annotation { "Feature Type Name" : "Feature", "Feature Type Description" : "" }
export const myFeature = defineFeature(function(context is Context, id is Id, definition is map)
    precondition{}
    {
        {
            var Q0;
            Q0=qCreatedBy(makeId("Top.planeOp"),FACE);
            var sketch = newSketch(context, id + "F0", { "sketchPlane" : qUnion([Q0])});
            skLineSegment(sketch, "E0.bottom", {"start": v(10900, -12400) * mm, "end": v(-10900, -12400) * mm});
            skLineSegment(sketch, "E0.top", {"start": v(10900, 12400) * mm, "end": v(-10900, 12400) * mm});
            skLineSegment(sketch, "E0.left", {"start": v(10900, -12400) * mm, "end": v(10900, 12400) * mm});
            skLineSegment(sketch, "E0.right", {"start": v(-10900, -12400) * mm, "end": v(-10900, 12400) * mm});
            skPoint(sketch, "E0.middle", {"position": v(0, 0) * mm});
            skSolve(sketch);
        }
        {
            var Q0;
            Q0=qSketchRegion(id+"F0",true);
            extrude(context, id + "F1", {"entities" : qUnion([Q0]), "depth" : 1000 * mm});
        }
        {
            var Q0;
            {var subQ2=sQuery(id+"FY67IvhjNhSzuPv_1.wireOp",EDGE,"VcfzDPvy-8ap2-iydv-9Ytp-1fS7yPx6LH9c.top");Q0=makeQuery(id+"FlI6K719u8TBiz5_1.boolean.opBoolean","SPLIT",FACE,{"disambiguationData":[TD([makeQuery(id+"FlI6K719u8TBiz5_1.opExtrude","SWEPT_FACE",FACE,{"disambiguationData":[OSD([subQ2])]})])],"derivedFrom":makeQuery(id+"F1.opExtrude","CAP_FACE",FACE,{"disambiguationData":[OSD([sQuery(id+"F0.wireOp",EDGE,"E0.bottom"),sQuery(id+"F0.wireOp",EDGE,"E0.top"),sQuery(id+"F0.wireOp",EDGE,"E0.left"),sQuery(id+"F0.wireOp",EDGE,"E0.right")])],"isStart":false})});}
            var sketch = newSketch(context, id + "F2", { "sketchPlane" : qUnion([Q0])});
            skLineSegment(sketch, "E1.bottom", {"start": v(10899.64, -12310) * mm, "end": v(-1650, -12310) * mm});
            skLineSegment(sketch, "E1.top", {"start": v(10899.64, 1690) * mm, "end": v(-1650, 1690) * mm});
            skLineSegment(sketch, "E1.left", {"start": v(10899.64, -12310) * mm, "end": v(10899.64, 1690) * mm});
            skLineSegment(sketch, "E1.right", {"start": v(-1650, -12310) * mm, "end": v(-1650, 1690) * mm});
            skSolve(sketch);
        }
        {
            var Q0;
            Q0=makeQuery(id+"F2.imprint","IMPRINT",FACE,{"disambiguationData":[TD([[makeQuery(id+"F2.imprint","IMPRINT",EDGE,{"derivedFrom":sQuery(id+"F2.wireOp",EDGE,"E1.bottom")}),1.0]])]});
            var sketch = newSketch(context, id + "F3", { "sketchPlane" : qUnion([Q0])});
            skLineSegment(sketch, "E2.bottom", {"start": v(-1560.36, 1600) * mm, "end": v(6439.64, 1600) * mm});
            skLineSegment(sketch, "E2.top", {"start": v(-1560.36, -2335.55) * mm, "end": v(6439.64, -2335.55) * mm});
            skLineSegment(sketch, "E2.left", {"start": v(-1560.36, 1600) * mm, "end": v(-1560.36, -2335.55) * mm});
            skLineSegment(sketch, "E2.right", {"start": v(6439.64, 1600) * mm, "end": v(6439.64, -2245.55) * mm});
            skLineSegment(sketch, "E3", {"start": v(6439.64, -2335.55) * mm, "end": v(10902.54, -2335.55) * mm});
            skLineSegment(sketch, "E4.bottom", {"start": v(-1560.36, 1600) * mm, "end": v(-10900, 1600) * mm});
            skLineSegment(sketch, "E4.top", {"start": v(-1560.36, -12400) * mm, "end": v(-10900, -12400) * mm});
            skLineSegment(sketch, "E4.left", {"start": v(-1560.36, 1600) * mm, "end": v(-1560.36, -12400) * mm});
            skLineSegment(sketch, "E4.right", {"start": v(-10900, 1600) * mm, "end": v(-10900, -12400) * mm});
            skLineSegment(sketch, "E5.bottom", {"start": v(-1560.36, -12400) * mm, "end": v(-4560.36, -12400) * mm});
            skLineSegment(sketch, "E5.left", {"start": v(-1560.36, -12400) * mm, "end": v(-1560.36, -9400) * mm});
            skLineSegment(sketch, "E6.bottom", {"start": v(-1470.36, 1510) * mm, "end": v(3259.64, 1510) * mm});
            skLineSegment(sketch, "E6.top", {"start": v(-1470.36, -2245.55) * mm, "end": v(3259.64, -2245.55) * mm});
            skLineSegment(sketch, "E6.left", {"start": v(-1470.36, 1510) * mm, "end": v(-1470.36, -2245.55) * mm});
            skLineSegment(sketch, "E6.right", {"start": v(6349.64, 1510) * mm, "end": v(6349.64, -2245.55) * mm});
            skLineSegment(sketch, "E7", {"start": v(3259.64, 1510) * mm, "end": v(3259.64, -2245.55) * mm});
            skLineSegment(sketch, "E8", {"start": v(3349.64, 1510) * mm, "end": v(3349.64, -2245.55) * mm});
            skLineSegment(sketch, "E9.trimOffspring", {"start": v(3349.64, -2245.55) * mm, "end": v(6349.64, -2245.55) * mm});
            skLineSegment(sketch, "E10.trimOffspring", {"start": v(3349.64, 1510) * mm, "end": v(6349.64, 1510) * mm});
            skLineSegment(sketch, "E11.bottom", {"start": v(6439.64, -2335.55) * mm, "end": v(10899.26, -2335.55) * mm});
            skLineSegment(sketch, "E11.top", {"start": v(6439.64, -2245.55) * mm, "end": v(10899.26, -2245.55) * mm});
            skLineSegment(sketch, "E11.right", {"start": v(10899.26, -2335.55) * mm, "end": v(10899.26, -2245.55) * mm});
            skLineSegment(sketch, "E12.bottom", {"start": v(-1560.36, 1600) * mm, "end": v(-4560.36, 1600) * mm});
            skLineSegment(sketch, "E12.left", {"start": v(-1560.36, 1600) * mm, "end": v(-1560.36, -400) * mm});
            skSolve(sketch);
        }
        {
            var Q0;
            Q0=qSketchRegion(id+"F3",true);
            extrude(context, id + "F4", {"entities" : qUnion([Q0]), "operationType" : NewBodyOperationType.ADD, "offsetDistance" : 25 * mm, "depth" : 4000 * mm});
        }
        {
            var Q0;
            Q0=makeQuery(id+"F4.opExtrude","CAP_FACE",FACE,{"disambiguationData":[OSD([sQuery(id+"F3.wireOp",EDGE,"E4.bottom"),sQuery(id+"F3.wireOp",EDGE,"E4.top"),sQuery(id+"F3.wireOp",EDGE,"E4.left"),sQuery(id+"F3.wireOp",EDGE,"E4.right"),sQuery(id+"F3.wireOp",EDGE,"E5.bottom"),sQuery(id+"F3.wireOp",EDGE,"E5.left"),sQuery(id+"F3.wireOp",EDGE,"E2.bottom"),sQuery(id+"F3.wireOp",EDGE,"E2.top"),sQuery(id+"F3.wireOp",EDGE,"E2.right"),sQuery(id+"F3.wireOp",EDGE,"E6.bottom"),sQuery(id+"F3.wireOp",EDGE,"E6.top"),sQuery(id+"F3.wireOp",EDGE,"E6.left"),sQuery(id+"F3.wireOp",EDGE,"E6.right"),sQuery(id+"F3.wireOp",EDGE,"E7"),sQuery(id+"F3.wireOp",EDGE,"E8"),sQuery(id+"F3.wireOp",EDGE,"E9.trimOffspring"),sQuery(id+"F3.wireOp",EDGE,"E10.trimOffspring"),sQuery(id+"F3.wireOp",EDGE,"E11.bottom"),sQuery(id+"F3.wireOp",EDGE,"E11.top"),sQuery(id+"F3.wireOp",EDGE,"E11.right"),sQuery(id+"F3.wireOp",EDGE,"E12.bottom")])],"isStart":false});
            var sketch = newSketch(context, id + "F5", { "sketchPlane" : qUnion([Q0])});
            skLineSegment(sketch, "E13.bottom", {"start": v(-1560.36, 1510) * mm, "end": v(-4560.36, 1510) * mm});
            skLineSegment(sketch, "E13.top", {"start": v(-1560.36, -990) * mm, "end": v(-4560.36, -990) * mm});
            skLineSegment(sketch, "E13.left", {"start": v(-1560.36, 1510) * mm, "end": v(-1560.36, -990) * mm});
            skLineSegment(sketch, "E13.right", {"start": v(-4560.36, 1510) * mm, "end": v(-4560.36, -990) * mm});
            skSolve(sketch);
        }
        {
            var Q0;
            Q0=qSketchRegion(id+"F5",true);
            extrude(context, id + "F6", {"entities" : qUnion([Q0]), "operationType" : NewBodyOperationType.REMOVE, "oppositeDirection" : true, "offsetDistance" : 25 * mm, "depth" : 4000 * mm});
        }
        {
            var Q0;
            Q0=makeQuery(id+"F4.opExtrude","CAP_FACE",FACE,{"disambiguationData":[OSD([sQuery(id+"F3.wireOp",EDGE,"E4.bottom"),sQuery(id+"F3.wireOp",EDGE,"E4.top"),sQuery(id+"F3.wireOp",EDGE,"E4.left"),sQuery(id+"F3.wireOp",EDGE,"E4.right"),sQuery(id+"F3.wireOp",EDGE,"E5.bottom"),sQuery(id+"F3.wireOp",EDGE,"E5.left"),sQuery(id+"F3.wireOp",EDGE,"E2.bottom"),sQuery(id+"F3.wireOp",EDGE,"E2.top"),sQuery(id+"F3.wireOp",EDGE,"E2.right"),sQuery(id+"F3.wireOp",EDGE,"E6.bottom"),sQuery(id+"F3.wireOp",EDGE,"E6.top"),sQuery(id+"F3.wireOp",EDGE,"E6.left"),sQuery(id+"F3.wireOp",EDGE,"E6.right"),sQuery(id+"F3.wireOp",EDGE,"E7"),sQuery(id+"F3.wireOp",EDGE,"E8"),sQuery(id+"F3.wireOp",EDGE,"E9.trimOffspring"),sQuery(id+"F3.wireOp",EDGE,"E10.trimOffspring"),sQuery(id+"F3.wireOp",EDGE,"E11.bottom"),sQuery(id+"F3.wireOp",EDGE,"E11.top"),sQuery(id+"F3.wireOp",EDGE,"E11.right"),sQuery(id+"F3.wireOp",EDGE,"E12.bottom")])],"isStart":false});
            var sketch = newSketch(context, id + "F7", { "sketchPlane" : qUnion([Q0])});
            skLineSegment(sketch, "E14", {"start": v(-4650.36, 1510) * mm, "end": v(-10810, 1510) * mm});
            skLineSegment(sketch, "E15", {"start": v(-1650.36, -9220) * mm, "end": v(-1650.36, -1080) * mm});
            skLineSegment(sketch, "E16", {"start": v(-1650.36, -1080) * mm, "end": v(-4650.36, -1080) * mm});
            skLineSegment(sketch, "E17", {"start": v(-4650.36, 1510) * mm, "end": v(-4650.36, -1080) * mm});
            skLineSegment(sketch, "E18", {"start": v(-7810, -12310) * mm, "end": v(-7810, -8310) * mm});
            skLineSegment(sketch, "E19", {"start": v(-7810, -8310) * mm, "end": v(-10810, -8310) * mm});
            skLineSegment(sketch, "E20", {"start": v(-7810, -12310) * mm, "end": v(-4650.36, -12310) * mm});
            skLineSegment(sketch, "E21", {"start": v(-10810, -8310) * mm, "end": v(-10810, 1510) * mm});
            skLineSegment(sketch, "E22", {"start": v(-1650.36, -9220) * mm, "end": v(-1650.36, -12310) * mm});
            skLineSegment(sketch, "E23", {"start": v(-1650.36, -12310) * mm, "end": v(-4650.36, -12310) * mm});
            skSolve(sketch);
        }
        {
            var Q0;
            Q0=qSketchRegion(id+"F7",true);
            extrude(context, id + "F8", {"entities" : qUnion([Q0]), "operationType" : NewBodyOperationType.REMOVE, "oppositeDirection" : true, "depth" : 4000 * mm});
        }
        {
            var Q0;
            Q0=makeQuery(id+"F4.opExtrude","CAP_FACE",FACE,{"disambiguationData":[OSD([sQuery(id+"F3.wireOp",EDGE,"E4.bottom"),sQuery(id+"F3.wireOp",EDGE,"E4.top"),sQuery(id+"F3.wireOp",EDGE,"E4.left"),sQuery(id+"F3.wireOp",EDGE,"E4.right"),sQuery(id+"F3.wireOp",EDGE,"E5.bottom"),sQuery(id+"F3.wireOp",EDGE,"E5.left"),sQuery(id+"F3.wireOp",EDGE,"E2.bottom"),sQuery(id+"F3.wireOp",EDGE,"E2.top"),sQuery(id+"F3.wireOp",EDGE,"E2.right"),sQuery(id+"F3.wireOp",EDGE,"E6.bottom"),sQuery(id+"F3.wireOp",EDGE,"E6.top"),sQuery(id+"F3.wireOp",EDGE,"E6.left"),sQuery(id+"F3.wireOp",EDGE,"E6.right"),sQuery(id+"F3.wireOp",EDGE,"E7"),sQuery(id+"F3.wireOp",EDGE,"E8"),sQuery(id+"F3.wireOp",EDGE,"E9.trimOffspring"),sQuery(id+"F3.wireOp",EDGE,"E10.trimOffspring"),sQuery(id+"F3.wireOp",EDGE,"E11.bottom"),sQuery(id+"F3.wireOp",EDGE,"E11.top"),sQuery(id+"F3.wireOp",EDGE,"E11.right"),sQuery(id+"F3.wireOp",EDGE,"E12.bottom")])],"isStart":false});
            var sketch = newSketch(context, id + "F9", { "sketchPlane" : qUnion([Q0])});
            skLineSegment(sketch, "E24.bottom", {"start": v(1849.64, 1600) * mm, "end": v(2669.64, 1600) * mm});
            skLineSegment(sketch, "E24.top", {"start": v(1849.64, 1510) * mm, "end": v(2669.64, 1510) * mm});
            skLineSegment(sketch, "E24.left", {"start": v(1849.64, 1600) * mm, "end": v(1849.64, 1510) * mm});
            skLineSegment(sketch, "E24.right", {"start": v(2669.64, 1600) * mm, "end": v(2669.64, 1510) * mm});
            skLineSegment(sketch, "E25.bottom", {"start": v(3259.64, -80) * mm, "end": v(3349.64, -80) * mm});
            skLineSegment(sketch, "E25.top", {"start": v(3259.64, -900) * mm, "end": v(3349.64, -900) * mm});
            skLineSegment(sketch, "E25.left", {"start": v(3259.64, -80) * mm, "end": v(3259.64, -900) * mm});
            skLineSegment(sketch, "E25.right", {"start": v(3349.64, -80) * mm, "end": v(3349.64, -900) * mm});
            skLineSegment(sketch, "E26.bottom", {"start": v(4439.64, 1600) * mm, "end": v(5259.64, 1600) * mm});
            skLineSegment(sketch, "E26.top", {"start": v(4439.64, 1510) * mm, "end": v(5259.64, 1510) * mm});
            skLineSegment(sketch, "E26.left", {"start": v(4439.64, 1600) * mm, "end": v(4439.64, 1510) * mm});
            skLineSegment(sketch, "E26.right", {"start": v(5259.64, 1600) * mm, "end": v(5259.64, 1510) * mm});
            skLineSegment(sketch, "E27.bottom", {"start": v(10399.64, -2335.55) * mm, "end": v(9579.64, -2335.55) * mm});
            skLineSegment(sketch, "E27.top", {"start": v(10399.64, -2245.55) * mm, "end": v(9579.64, -2245.55) * mm});
            skLineSegment(sketch, "E27.left", {"start": v(10399.64, -2335.55) * mm, "end": v(10399.64, -2245.55) * mm});
            skLineSegment(sketch, "E27.right", {"start": v(9579.64, -2335.55) * mm, "end": v(9579.64, -2245.55) * mm});
            skLineSegment(sketch, "E28.bottom", {"start": v(-3880.36, -990) * mm, "end": v(-2240.36, -990) * mm});
            skLineSegment(sketch, "E28.top", {"start": v(-3880.36, -1080) * mm, "end": v(-2240.36, -1080) * mm});
            skLineSegment(sketch, "E28.left", {"start": v(-3880.36, -990) * mm, "end": v(-3880.36, -1080) * mm});
            skLineSegment(sketch, "E28.right", {"start": v(-2240.36, -990) * mm, "end": v(-2240.36, -1080) * mm});
            skLineSegment(sketch, "E29.bottom", {"start": v(-2250.36, 1510) * mm, "end": v(-3870.36, 1510) * mm});
            skLineSegment(sketch, "E29.top", {"start": v(-2250.36, 1600) * mm, "end": v(-3870.36, 1600) * mm});
            skLineSegment(sketch, "E29.left", {"start": v(-2250.36, 1510) * mm, "end": v(-2250.36, 1600) * mm});
            skLineSegment(sketch, "E29.right", {"start": v(-3870.36, 1510) * mm, "end": v(-3870.36, 1600) * mm});
            skLineSegment(sketch, "E30.bottom", {"start": v(-8410, -8310) * mm, "end": v(-9230, -8310) * mm});
            skLineSegment(sketch, "E30.top", {"start": v(-8410, -8400) * mm, "end": v(-9230, -8400) * mm});
            skLineSegment(sketch, "E30.left", {"start": v(-8410, -8310) * mm, "end": v(-8410, -8400) * mm});
            skLineSegment(sketch, "E30.right", {"start": v(-9230, -8310) * mm, "end": v(-9230, -8400) * mm});
            skPoint(sketch, "E31", {"position": v(2259.64, 1510) * mm});
            skPoint(sketch, "E32", {"position": v(4849.64, 1510) * mm});
            skPoint(sketch, "E33", {"position": v(3259.64, -490) * mm});
            skPoint(sketch, "E34", {"position": v(-3060.36, -990) * mm});
            skPoint(sketch, "E35", {"position": v(-3060.36, 1510) * mm});
            skPoint(sketch, "E36", {"position": v(-8820, -8400) * mm});
            skLineSegment(sketch, "E37", {"start": v(-7810, -8310) * mm, "end": v(-8410, -8310) * mm, "construction": true});
            skSolve(sketch);
        }
        {
            var Q0;
            Q0=qSketchRegion(id+"F9",true);
            extrude(context, id + "F10", {"entities" : qUnion([Q0]), "operationType" : NewBodyOperationType.REMOVE, "oppositeDirection" : true, "depth" : 4000 * mm});
        }
        {
            var Q0;
            Q0=makeQuery(id+"F2.imprint","IMPRINT",FACE,{"disambiguationData":[TD([[makeQuery(id+"F2.imprint","IMPRINT",EDGE,{"derivedFrom":sQuery(id+"F2.wireOp",EDGE,"E1.bottom")}),1.0]])]});
            var sketch = newSketch(context, id + "F11", { "sketchPlane" : qUnion([Q0])});
            skText(sketch, "E38", { "text": "Breakout Room", "fontName": "OpenSans-Regular.ttf"});
            skText(sketch, "E39", { "text": "SLS Area", "fontName": "OpenSans-Regular.ttf"});
            skText(sketch, "E40", { "text": "Post Processing\nfor SLS", "fontName": "OpenSans-Regular.ttf"});
            const initialGuessF11  = {"E38": [-0.56036, -7.09274, 1, 0, 0.73998], "E39": [-0.56036, 6.4231, 1, 0, 1.60528], "E40": [-9.9, 7.677, 1, 0, 0.35138]};
            skSetInitialGuess(sketch, initialGuessF11);
            skSolve(sketch);
        }
        {
            var Q0;
            Q0 = qSketchRegion(id + "F11", true);
            extrude(context, id + "F12", {"entities" : qUnion([Q0]), "operationType" : NewBodyOperationType.REMOVE, "oppositeDirection" : true, "depth" : 500 * mm});
        }
        {
            var Q0;
            Q0=makeQuery(id+"F2.imprint","IMPRINT",FACE,{"disambiguationData":[TD([[makeQuery(id+"F2.imprint","IMPRINT",EDGE,{"derivedFrom":sQuery(id+"F2.wireOp",EDGE,"E1.bottom")}),-1.0]])]});
            var sketch = newSketch(context, id + "F13", { "sketchPlane" : qUnion([Q0])});
            skLineSegment(sketch, "E41.bottom", {"start": v(10899.64, -5985) * mm, "end": v(8004.64, -5985) * mm});
            skLineSegment(sketch, "E41.top", {"start": v(10899.64, -12400) * mm, "end": v(8004.64, -12400) * mm});
            skLineSegment(sketch, "E41.left", {"start": v(10899.64, -5985) * mm, "end": v(10899.64, -12400) * mm});
            skLineSegment(sketch, "E41.right", {"start": v(8004.64, -5985) * mm, "end": v(8004.64, -9872.88) * mm});
            skLineSegment(sketch, "E42.bottom", {"start": v(8004.64, -9872.88) * mm, "end": v(4084.64, -9872.88) * mm});
            skLineSegment(sketch, "E42.top", {"start": v(8701.5, -12400) * mm, "end": v(4084.64, -12400) * mm});
            skLineSegment(sketch, "E42.right", {"start": v(4084.64, -9872.88) * mm, "end": v(4084.64, -12400) * mm});
            skLineSegment(sketch, "E43.bottom", {"start": v(8094.64, -6075) * mm, "end": v(10809.64, -6075) * mm});
            skLineSegment(sketch, "E43.top", {"start": v(8094.64, -12310) * mm, "end": v(10809.64, -12310) * mm});
            skLineSegment(sketch, "E43.left", {"start": v(8094.64, -6075) * mm, "end": v(8094.64, -12310) * mm});
            skLineSegment(sketch, "E43.right", {"start": v(10809.64, -6075) * mm, "end": v(10809.64, -12310) * mm});
            skLineSegment(sketch, "E44.bottom", {"start": v(4174.64, -9962.88) * mm, "end": v(5624.64, -9962.88) * mm});
            skLineSegment(sketch, "E44.top", {"start": v(4174.64, -12310) * mm, "end": v(5624.64, -12310) * mm});
            skLineSegment(sketch, "E44.left", {"start": v(4174.64, -9962.88) * mm, "end": v(4174.64, -12310) * mm});
            skLineSegment(sketch, "E44.right", {"start": v(5624.64, -9962.88) * mm, "end": v(5624.64, -12310) * mm});
            skLineSegment(sketch, "E45.bottom", {"start": v(5714.64, -9962.88) * mm, "end": v(8004.64, -9962.88) * mm});
            skLineSegment(sketch, "E45.top", {"start": v(5714.64, -12310) * mm, "end": v(8004.64, -12310) * mm});
            skLineSegment(sketch, "E45.left", {"start": v(5714.64, -9962.88) * mm, "end": v(5714.64, -12310) * mm});
            skLineSegment(sketch, "E45.right", {"start": v(8004.64, -9962.88) * mm, "end": v(8004.64, -12310) * mm});
            skSolve(sketch);
        }
        {
            var Q0;
            Q0 = qSketchRegion(id + "F13", true);
            extrude(context, id + "F14", {"entities" : qUnion([Q0]), "operationType" : NewBodyOperationType.ADD, "depth" : 4000 * mm});
        }
        {
            var Q0;
            Q0=makeQuery(id+"F2.imprint","IMPRINT",FACE,{"disambiguationData":[TD([[makeQuery(id+"F2.imprint","IMPRINT",EDGE,{"derivedFrom":sQuery(id+"F2.wireOp",EDGE,"E1.bottom")}),-1.0]])]});
            var sketch = newSketch(context, id + "F15", { "sketchPlane" : qUnion([Q0])});
            skLineSegment(sketch, "E46.bottom", {"start": v(4084.64, -9872.88) * mm, "end": v(3384.64, -9872.88) * mm});
            skLineSegment(sketch, "E46.top", {"start": v(4084.64, -12400) * mm, "end": v(3384.64, -12400) * mm});
            skLineSegment(sketch, "E46.left", {"start": v(4084.64, -9872.88) * mm, "end": v(4084.64, -12400) * mm});
            skLineSegment(sketch, "E46.right", {"start": v(3384.64, -9872.88) * mm, "end": v(3384.64, -12400) * mm});
            skSolve(sketch);
        }
        {
            var Q0;
            Q0 = qSketchRegion(id + "F15", true);
            extrude(context, id + "F16", {"entities" : qUnion([Q0]), "operationType" : NewBodyOperationType.ADD, "depth" : 1250 * mm});
        }
        {
            var Q0;
            Q0=makeQuery(id+"F2.imprint","IMPRINT",FACE,{"disambiguationData":[TD([[makeQuery(id+"F2.imprint","IMPRINT",EDGE,{"derivedFrom":sQuery(id+"F2.wireOp",EDGE,"E1.bottom")}),1.0]])]});
            var sketch = newSketch(context, id + "F17", { "sketchPlane" : qUnion([Q0])});
            skLineSegment(sketch, "E47.bottom", {"start": v(-10900, 1600) * mm, "end": v(-10810, 1600) * mm});
            skLineSegment(sketch, "E47.top", {"start": v(-10900, 12400) * mm, "end": v(-10810, 12400) * mm});
            skLineSegment(sketch, "E47.left", {"start": v(-10900, 1600) * mm, "end": v(-10900, 12400) * mm});
            skLineSegment(sketch, "E47.right", {"start": v(-10810, 1600) * mm, "end": v(-10810, 12310) * mm});
            skLineSegment(sketch, "E48.bottom", {"start": v(-10810, 12400) * mm, "end": v(10900, 12400) * mm});
            skLineSegment(sketch, "E48.top", {"start": v(-10810, 12310) * mm, "end": v(10810, 12310) * mm});
            skLineSegment(sketch, "E48.right", {"start": v(10900, 12400) * mm, "end": v(10900, 12310) * mm});
            skLineSegment(sketch, "E49.top", {"start": v(10900, -5985) * mm, "end": v(10810, -5985) * mm});
            skLineSegment(sketch, "E49.left", {"start": v(10900, 12310) * mm, "end": v(10900, -5985) * mm});
            skLineSegment(sketch, "E49.right", {"start": v(10810, 12310) * mm, "end": v(10810, -5985) * mm});
            skLineSegment(sketch, "E50.bottom", {"start": v(4084.64, -12310) * mm, "end": v(-1560.36, -12310) * mm});
            skLineSegment(sketch, "E50.top", {"start": v(4084.64, -12400) * mm, "end": v(-1560.36, -12400) * mm});
            skLineSegment(sketch, "E50.left", {"start": v(4084.64, -12310) * mm, "end": v(4084.64, -12400) * mm});
            skLineSegment(sketch, "E50.right", {"start": v(-1560.36, -12310) * mm, "end": v(-1560.36, -12400) * mm});
            skSolve(sketch);
        }
        {
            var Q0;
            Q0 = qSketchRegion(id + "F17", true);
            extrude(context, id + "F18", {"entities" : qUnion([Q0]), "operationType" : NewBodyOperationType.ADD, "depth" : 4000 * mm});
        }
        {
            var Q0;
            {var subQ0=sQuery(id+"F3.wireOp",EDGE,"E11.top");var subQ2=sQuery(id+"F3.wireOp",EDGE,"E10.trimOffspring");var subQ3=sQuery(id+"F3.wireOp",EDGE,"E9.trimOffspring");var subQ4=sQuery(id+"F3.wireOp",EDGE,"E8");var subQ5=sQuery(id+"F3.wireOp",EDGE,"E7");var subQ6=sQuery(id+"F3.wireOp",EDGE,"E6.right");var subQ7=sQuery(id+"F3.wireOp",EDGE,"E6.left");var subQ8=sQuery(id+"F3.wireOp",EDGE,"E5.bottom");var subQ9=sQuery(id+"F3.wireOp",EDGE,"E4.top");var subQ10=sQuery(id+"F3.wireOp",EDGE,"E12.bottom");var subQ11=sQuery(id+"F3.wireOp",EDGE,"E2.bottom");var subQ12=sQuery(id+"F3.wireOp",EDGE,"E4.bottom");var subQ13=sQuery(id+"F3.wireOp",EDGE,"E2.right");var subQ14=sQuery(id+"F3.wireOp",EDGE,"E5.left");var subQ15=sQuery(id+"F3.wireOp",EDGE,"E4.left");var subQ16=sQuery(id+"F3.wireOp",EDGE,"E4.right");var subQ17=sQuery(id+"F3.wireOp",EDGE,"E11.bottom");var subQ18=sQuery(id+"F3.wireOp",EDGE,"E2.top");var subQ20=sQuery(id+"F3.wireOp",EDGE,"E6.bottom");var subQ21=sQuery(id+"F3.wireOp",EDGE,"E6.top");var subQ22=sQuery(id+"F3.wireOp",EDGE,"E11.right");var subQ23=makeQuery(id+"F4.opExtrude","CAP_FACE",FACE,{"disambiguationData":[OSD([subQ12,subQ9,subQ15,subQ16,subQ8,subQ14,subQ11,subQ18,subQ13,subQ20,subQ21,subQ7,subQ6,subQ5,subQ4,subQ3,subQ2,subQ17,subQ0,subQ22,subQ10])],"isStart":false});Q0=makeQuery(id+"F18.boolean.opBoolean","MERGE",FACE,{"derivedFrom":[makeQuery(id+"F10.boolean.opBoolean","SPLIT",FACE,{"disambiguationData":[TD([makeQuery(id+"F4.opExtrude","SWEPT_FACE",FACE,{"disambiguationData":[OSD([subQ22])]})])],"derivedFrom":subQ23}),makeQuery(id+"F10.boolean.opBoolean","SPLIT",FACE,{"disambiguationData":[TD([makeQuery(id+"F1.opExtrude","SWEPT_FACE",FACE,{"disambiguationData":[OSD([sQuery(id+"F0.wireOp",EDGE,"E0.bottom")])]})])],"derivedFrom":subQ23}),makeQuery(id+"F14.opExtrude","CAP_FACE",FACE,{"disambiguationData":[OSD([sQuery(id+"F13.wireOp",EDGE,"E41.bottom"),sQuery(id+"F13.wireOp",EDGE,"E41.top"),sQuery(id+"F13.wireOp",EDGE,"E41.left"),sQuery(id+"F13.wireOp",EDGE,"E41.right"),sQuery(id+"F13.wireOp",EDGE,"E42.bottom"),sQuery(id+"F13.wireOp",EDGE,"E42.top"),sQuery(id+"F13.wireOp",EDGE,"E42.right"),sQuery(id+"F13.wireOp",EDGE,"E43.bottom"),sQuery(id+"F13.wireOp",EDGE,"E43.top"),sQuery(id+"F13.wireOp",EDGE,"E43.left"),sQuery(id+"F13.wireOp",EDGE,"E43.right"),sQuery(id+"F13.wireOp",EDGE,"E44.bottom"),sQuery(id+"F13.wireOp",EDGE,"E44.top"),sQuery(id+"F13.wireOp",EDGE,"E44.left"),sQuery(id+"F13.wireOp",EDGE,"E44.right"),sQuery(id+"F13.wireOp",EDGE,"E45.bottom"),sQuery(id+"F13.wireOp",EDGE,"E45.top"),sQuery(id+"F13.wireOp",EDGE,"E45.left"),sQuery(id+"F13.wireOp",EDGE,"E45.right")])],"isStart":false}),makeQuery(id+"F18.opExtrude","CAP_FACE",FACE,{"disambiguationData":[OSD([sQuery(id+"F17.wireOp",EDGE,"E47.bottom"),sQuery(id+"F17.wireOp",EDGE,"E47.top"),sQuery(id+"F17.wireOp",EDGE,"E47.left"),sQuery(id+"F17.wireOp",EDGE,"E47.right"),sQuery(id+"F17.wireOp",EDGE,"E48.bottom"),sQuery(id+"F17.wireOp",EDGE,"E48.top"),sQuery(id+"F17.wireOp",EDGE,"E48.right"),sQuery(id+"F17.wireOp",EDGE,"E49.top"),sQuery(id+"F17.wireOp",EDGE,"E49.left"),sQuery(id+"F17.wireOp",EDGE,"E49.right")])],"isStart":false}),makeQuery(id+"F18.opExtrude","CAP_FACE",FACE,{"disambiguationData":[OSD([sQuery(id+"F17.wireOp",EDGE,"E50.bottom"),sQuery(id+"F17.wireOp",EDGE,"E50.top"),sQuery(id+"F17.wireOp",EDGE,"E50.left"),sQuery(id+"F17.wireOp",EDGE,"E50.right")])],"isStart":false})]});}
            var sketch = newSketch(context, id + "F19", { "sketchPlane" : qUnion([Q0])});
            skLineSegment(sketch, "E51.bottom", {"start": v(10809.64, -6675) * mm, "end": v(10899.64, -6675) * mm});
            skLineSegment(sketch, "E51.top", {"start": v(10809.64, -8425) * mm, "end": v(10899.64, -8425) * mm});
            skLineSegment(sketch, "E51.left", {"start": v(10809.64, -6675) * mm, "end": v(10809.64, -8425) * mm});
            skLineSegment(sketch, "E51.right", {"start": v(10899.64, -6675) * mm, "end": v(10899.64, -8425) * mm});
            skLineSegment(sketch, "E52.bottom", {"start": v(10900, 11635) * mm, "end": v(10810, 11635) * mm});
            skLineSegment(sketch, "E52.top", {"start": v(10900, 6635) * mm, "end": v(10810, 6635) * mm});
            skLineSegment(sketch, "E52.left", {"start": v(10900, 11635) * mm, "end": v(10900, 6635) * mm});
            skLineSegment(sketch, "E52.right", {"start": v(10810, 11635) * mm, "end": v(10810, 6635) * mm});
            skLineSegment(sketch, "E53.bottom", {"start": v(10810, 3190) * mm, "end": v(10900, 3190) * mm});
            skLineSegment(sketch, "E53.top", {"start": v(10810, 3840) * mm, "end": v(10900, 3840) * mm});
            skLineSegment(sketch, "E53.left", {"start": v(10810, 3190) * mm, "end": v(10810, 3840) * mm});
            skLineSegment(sketch, "E53.right", {"start": v(10900, 3190) * mm, "end": v(10900, 3840) * mm});
            skLineSegment(sketch, "E54.bottom", {"start": v(8004.64, -6675) * mm, "end": v(8094.64, -6675) * mm});
            skLineSegment(sketch, "E54.top", {"start": v(8004.64, -8425) * mm, "end": v(8094.64, -8425) * mm});
            skLineSegment(sketch, "E54.left", {"start": v(8004.64, -6675) * mm, "end": v(8004.64, -8425) * mm});
            skLineSegment(sketch, "E54.right", {"start": v(8094.64, -6675) * mm, "end": v(8094.64, -8425) * mm});
            skPoint(sketch, "E55.oppositeSnap0", {"position": v(6859.64, -9962.88) * mm});
            skLineSegment(sketch, "E55.bottom", {"start": v(6059.64, -9962.88) * mm, "end": v(6859.64, -9962.88) * mm});
            skLineSegment(sketch, "E55.top", {"start": v(6059.64, -9872.88) * mm, "end": v(6859.64, -9872.88) * mm});
            skLineSegment(sketch, "E55.left", {"start": v(6059.64, -9962.88) * mm, "end": v(6059.64, -9872.88) * mm});
            skLineSegment(sketch, "E55.right", {"start": v(6859.64, -9962.88) * mm, "end": v(6859.64, -9872.88) * mm});
            skLineSegment(sketch, "E56.bottom", {"start": v(5524.64, -9962.88) * mm, "end": v(4724.64, -9962.88) * mm});
            skLineSegment(sketch, "E56.top", {"start": v(5524.64, -9872.88) * mm, "end": v(4724.64, -9872.88) * mm});
            skLineSegment(sketch, "E56.left", {"start": v(5524.64, -9962.88) * mm, "end": v(5524.64, -9872.88) * mm});
            skLineSegment(sketch, "E56.right", {"start": v(4724.64, -9962.88) * mm, "end": v(4724.64, -9872.88) * mm});
            skSolve(sketch);
        }
        {
            var Q0;
            Q0 = qSketchRegion(id + "F19", true);
            extrude(context, id + "F20", {"entities" : qUnion([Q0]), "operationType" : NewBodyOperationType.REMOVE, "oppositeDirection" : true, "depth" : 4000 * mm});
        }
        {
            var Q0;
            Q0=makeQuery(id+"F2.imprint","IMPRINT",FACE,{"disambiguationData":[TD([[makeQuery(id+"F2.imprint","IMPRINT",EDGE,{"derivedFrom":sQuery(id+"F2.wireOp",EDGE,"E1.bottom")}),-1.0]])]});
            var sketch = newSketch(context, id + "F21", { "sketchPlane" : qUnion([Q0])});
            skSolve(sketch);
        }
        {
            var Q0;
            {var subQ2=sQuery(id+"F17.wireOp",EDGE,"E50.bottom");var subQ4=sQuery(id+"F17.wireOp",EDGE,"E49.right");var subQ6=sQuery(id+"F17.wireOp",EDGE,"E49.left");var subQ7=sQuery(id+"F17.wireOp",EDGE,"E48.right");var subQ9=sQuery(id+"F17.wireOp",EDGE,"E47.right");var subQ13=makeQuery(id+"F1.opExtrude","SWEPT_FACE",FACE,{"disambiguationData":[OSD([sQuery(id+"F0.wireOp",EDGE,"E0.bottom")])]});var subQ17=sQuery(id+"F13.wireOp",EDGE,"E43.left");var subQ19=sQuery(id+"F13.wireOp",EDGE,"E43.top");var subQ22=sQuery(id+"F13.wireOp",EDGE,"E42.bottom");var subQ25=sQuery(id+"F13.wireOp",EDGE,"E41.right");var subQ26=sQuery(id+"F3.wireOp",EDGE,"E5.left");var subQ27=sQuery(id+"F3.wireOp",EDGE,"E4.left");var subQ30=sQuery(id+"F3.wireOp",EDGE,"E5.bottom");var subQ31=sQuery(id+"F3.wireOp",EDGE,"E4.top");var subQ33=sQuery(id+"F3.wireOp",EDGE,"E12.bottom");var subQ34=sQuery(id+"F3.wireOp",EDGE,"E2.bottom");var subQ35=sQuery(id+"F3.wireOp",EDGE,"E4.bottom");var subQ39=sQuery(id+"F13.wireOp",EDGE,"E41.left");var subQ41=sQuery(id+"F17.wireOp",EDGE,"E50.top");var subQ43=sQuery(id+"F13.wireOp",EDGE,"E42.top");var subQ44=sQuery(id+"F13.wireOp",EDGE,"E41.top");var subQ45=sQuery(id+"F3.wireOp",EDGE,"E2.right");var subQ49=sQuery(id+"F3.wireOp",EDGE,"E11.bottom");var subQ50=sQuery(id+"F3.wireOp",EDGE,"E2.top");var subQ52=sQuery(id+"F3.wireOp",EDGE,"E4.right");var subQ55=sQuery(id+"F3.wireOp",EDGE,"E6.bottom");var subQ57=sQuery(id+"F3.wireOp",EDGE,"E6.top");var subQ59=sQuery(id+"F3.wireOp",EDGE,"E6.left");var subQ61=sQuery(id+"F3.wireOp",EDGE,"E6.right");var subQ63=sQuery(id+"F3.wireOp",EDGE,"E7");var subQ65=sQuery(id+"F3.wireOp",EDGE,"E8");var subQ67=sQuery(id+"F3.wireOp",EDGE,"E9.trimOffspring");var subQ70=sQuery(id+"F3.wireOp",EDGE,"E10.trimOffspring");var subQ72=sQuery(id+"F3.wireOp",EDGE,"E11.top");var subQ76=sQuery(id+"F13.wireOp",EDGE,"E42.right");var subQ77=sQuery(id+"F13.wireOp",EDGE,"E43.right");var subQ78=sQuery(id+"F13.wireOp",EDGE,"E44.bottom");var subQ79=sQuery(id+"F13.wireOp",EDGE,"E44.top");var subQ80=sQuery(id+"F13.wireOp",EDGE,"E44.left");var subQ81=sQuery(id+"F13.wireOp",EDGE,"E44.right");var subQ82=sQuery(id+"F13.wireOp",EDGE,"E45.bottom");var subQ83=sQuery(id+"F13.wireOp",EDGE,"E45.top");var subQ84=sQuery(id+"F13.wireOp",EDGE,"E45.left");var subQ85=sQuery(id+"F13.wireOp",EDGE,"E45.right");var subQ86=sQuery(id+"F17.wireOp",EDGE,"E48.bottom");var subQ87=sQuery(id+"F17.wireOp",EDGE,"E47.top");var subQ88=sQuery(id+"F17.wireOp",EDGE,"E47.left");var subQ89=sQuery(id+"F17.wireOp",EDGE,"E48.top");var subQ90=sQuery(id+"F3.wireOp",EDGE,"E11.right");var subQ91=makeQuery(id+"F4.opExtrude","CAP_FACE",FACE,{"disambiguationData":[OSD([subQ35,subQ31,subQ27,subQ52,subQ30,subQ26,subQ34,subQ50,subQ45,subQ55,subQ57,subQ59,subQ61,subQ63,subQ65,subQ67,subQ70,subQ49,subQ72,subQ90,subQ33])],"isStart":false});Q0=makeQuery(id+"F6zr4ULHS1r3a6V_1.boolean.opBoolean","MERGE",FACE,{"derivedFrom":[makeQuery(id+"F20.boolean.opBoolean","SPLIT",FACE,{"disambiguationData":[TD([subQ13])],"derivedFrom":makeQuery(id+"F18.boolean.opBoolean","MERGE",FACE,{"derivedFrom":[makeQuery(id+"F10.boolean.opBoolean","SPLIT",FACE,{"disambiguationData":[TD([makeQuery(id+"F4.opExtrude","SWEPT_FACE",FACE,{"disambiguationData":[OSD([subQ90])]})])],"derivedFrom":subQ91}),makeQuery(id+"F10.boolean.opBoolean","SPLIT",FACE,{"disambiguationData":[TD([subQ13])],"derivedFrom":subQ91}),makeQuery(id+"F14.opExtrude","CAP_FACE",FACE,{"disambiguationData":[OSD([sQuery(id+"F13.wireOp",EDGE,"E41.bottom"),subQ44,subQ39,subQ25,subQ22,subQ43,subQ76,sQuery(id+"F13.wireOp",EDGE,"E43.bottom"),subQ19,subQ17,subQ77,subQ78,subQ79,subQ80,subQ81,subQ82,subQ83,subQ84,subQ85])],"isStart":false}),makeQuery(id+"F18.opExtrude","CAP_FACE",FACE,{"disambiguationData":[OSD([sQuery(id+"F17.wireOp",EDGE,"E47.bottom"),subQ87,subQ88,subQ9,subQ86,subQ89,subQ7,sQuery(id+"F17.wireOp",EDGE,"E49.top"),subQ6,subQ4])],"isStart":false}),makeQuery(id+"F18.opExtrude","CAP_FACE",FACE,{"disambiguationData":[OSD([subQ2,subQ41,sQuery(id+"F17.wireOp",EDGE,"E50.left"),sQuery(id+"F17.wireOp",EDGE,"E50.right")])],"isStart":false})]})}),makeQuery(id+"F6zr4ULHS1r3a6V_1.opExtrude","CAP_FACE",FACE,{"disambiguationData":[OSD([sQuery(id+"F21.wireOp",EDGE,"3vJUyLjv-637K-8uJn-XcPZ-ryVCrB70G0wa"),sQuery(id+"F21.wireOp",EDGE,"fNZKC1t2-5dP1-KvF3-ekiq-EYq1SIMscEtA"),sQuery(id+"F21.wireOp",EDGE,"6fOknZEH-1iJW-kcCI-w2z6-zF9aPqN6gvis"),sQuery(id+"F21.wireOp",EDGE,"bTZfj5QQ-9lIJ-ZMQn-vdRy-Df5yeWs6KGNL"),sQuery(id+"F21.wireOp",EDGE,"HPHwNwoX-cHC2-jXp5-qCgU-TAMVVla6UKj8"),sQuery(id+"F21.wireOp",EDGE,"Pcy1QBbd-VQnp-UDdW-fNgy-PcfSoAW424Jd")])],"isStart":false})]});}
            var sketch = newSketch(context, id + "F22", { "sketchPlane" : qUnion([Q0])});
            skLineSegment(sketch, "E57.bottom", {"start": v(-5069.45, 1510) * mm, "end": v(-6669.45, 1510) * mm});
            skLineSegment(sketch, "E57.top", {"start": v(-5069.45, 1600) * mm, "end": v(-6669.45, 1600) * mm});
            skLineSegment(sketch, "E57.left", {"start": v(-5069.45, 1510) * mm, "end": v(-5069.45, 1600) * mm});
            skLineSegment(sketch, "E57.right", {"start": v(-6669.45, 1510) * mm, "end": v(-6669.45, 1600) * mm});
            skSolve(sketch);
        }
        {
            var Q0;
            Q0 = qSketchRegion(id + "F22", true);
            extrude(context, id + "F23", {"entities" : qUnion([Q0]), "operationType" : NewBodyOperationType.REMOVE, "oppositeDirection" : true, "offsetDistance" : 25 * mm, "depth" : 4000 * mm});
        }
        {
            var Q0;
            {var subQ0=sQuery(id+"F13.wireOp",EDGE,"E43.top");var subQ7=sQuery(id+"F17.wireOp",EDGE,"E49.right");var subQ11=sQuery(id+"F17.wireOp",EDGE,"E49.left");var subQ12=sQuery(id+"F17.wireOp",EDGE,"E48.right");var subQ16=sQuery(id+"F17.wireOp",EDGE,"E47.right");var subQ19=sQuery(id+"F13.wireOp",EDGE,"E44.left");var subQ24=makeQuery(id+"F1.opExtrude","SWEPT_FACE",FACE,{"disambiguationData":[OSD([sQuery(id+"F0.wireOp",EDGE,"E0.bottom")])]});var subQ25=sQuery(id+"F13.wireOp",EDGE,"E43.left");var subQ29=sQuery(id+"F13.wireOp",EDGE,"E42.bottom");var subQ31=sQuery(id+"F3.wireOp",EDGE,"E5.left");var subQ32=sQuery(id+"F3.wireOp",EDGE,"E4.left");var subQ34=sQuery(id+"F13.wireOp",EDGE,"E43.right");var subQ38=sQuery(id+"F3.wireOp",EDGE,"E5.bottom");var subQ39=sQuery(id+"F3.wireOp",EDGE,"E4.top");var subQ41=sQuery(id+"F3.wireOp",EDGE,"E12.bottom");var subQ42=sQuery(id+"F3.wireOp",EDGE,"E2.bottom");var subQ43=sQuery(id+"F3.wireOp",EDGE,"E4.bottom");var subQ46=sQuery(id+"F13.wireOp",EDGE,"E41.left");var subQ49=sQuery(id+"F13.wireOp",EDGE,"E42.top");var subQ50=sQuery(id+"F13.wireOp",EDGE,"E41.top");var subQ52=sQuery(id+"F3.wireOp",EDGE,"E2.right");var subQ54=sQuery(id+"F13.wireOp",EDGE,"E44.top");var subQ58=sQuery(id+"F3.wireOp",EDGE,"E11.bottom");var subQ59=sQuery(id+"F3.wireOp",EDGE,"E2.top");var subQ61=sQuery(id+"F3.wireOp",EDGE,"E4.right");var subQ63=sQuery(id+"F13.wireOp",EDGE,"E44.bottom");var subQ66=sQuery(id+"F3.wireOp",EDGE,"E6.bottom");var subQ68=sQuery(id+"F3.wireOp",EDGE,"E6.top");var subQ70=sQuery(id+"F3.wireOp",EDGE,"E6.left");var subQ72=sQuery(id+"F3.wireOp",EDGE,"E6.right");var subQ74=sQuery(id+"F3.wireOp",EDGE,"E7");var subQ76=sQuery(id+"F13.wireOp",EDGE,"E41.right");var subQ78=sQuery(id+"F3.wireOp",EDGE,"E8");var subQ80=sQuery(id+"F3.wireOp",EDGE,"E9.trimOffspring");var subQ82=sQuery(id+"F13.wireOp",EDGE,"E42.right");var subQ84=sQuery(id+"F3.wireOp",EDGE,"E10.trimOffspring");var subQ86=sQuery(id+"F3.wireOp",EDGE,"E11.top");var subQ91=sQuery(id+"F13.wireOp",EDGE,"E44.right");var subQ93=sQuery(id+"F13.wireOp",EDGE,"E45.bottom");var subQ95=sQuery(id+"F13.wireOp",EDGE,"E45.top");var subQ97=sQuery(id+"F13.wireOp",EDGE,"E45.left");var subQ99=sQuery(id+"F13.wireOp",EDGE,"E45.right");var subQ103=sQuery(id+"F17.wireOp",EDGE,"E48.bottom");var subQ104=sQuery(id+"F17.wireOp",EDGE,"E47.top");var subQ106=sQuery(id+"F17.wireOp",EDGE,"E47.left");var subQ108=sQuery(id+"F17.wireOp",EDGE,"E48.top");var subQ110=sQuery(id+"F17.wireOp",EDGE,"E50.bottom");var subQ112=sQuery(id+"F17.wireOp",EDGE,"E50.top");var subQ125=sQuery(id+"F3.wireOp",EDGE,"E11.right");var subQ126=makeQuery(id+"F4.opExtrude","CAP_FACE",FACE,{"disambiguationData":[OSD([subQ43,subQ39,subQ32,subQ61,subQ38,subQ31,subQ42,subQ59,subQ52,subQ66,subQ68,subQ70,subQ72,subQ74,subQ78,subQ80,subQ84,subQ58,subQ86,subQ125,subQ41])],"isStart":false});Q0=makeQuery(id+"F23.boolean.opBoolean","SPLIT",FACE,{"disambiguationData":[TD([subQ24])],"derivedFrom":makeQuery(id+"F20.boolean.opBoolean","SPLIT",FACE,{"disambiguationData":[TD([subQ24])],"derivedFrom":makeQuery(id+"F18.boolean.opBoolean","MERGE",FACE,{"derivedFrom":[makeQuery(id+"F10.boolean.opBoolean","SPLIT",FACE,{"disambiguationData":[TD([makeQuery(id+"F4.opExtrude","SWEPT_FACE",FACE,{"disambiguationData":[OSD([subQ125])]})])],"derivedFrom":subQ126}),makeQuery(id+"F10.boolean.opBoolean","SPLIT",FACE,{"disambiguationData":[TD([subQ24])],"derivedFrom":subQ126}),makeQuery(id+"F14.opExtrude","CAP_FACE",FACE,{"disambiguationData":[OSD([sQuery(id+"F13.wireOp",EDGE,"E41.bottom"),subQ50,subQ46,subQ76,subQ29,subQ49,subQ82,sQuery(id+"F13.wireOp",EDGE,"E43.bottom"),subQ0,subQ25,subQ34,subQ63,subQ54,subQ19,subQ91,subQ93,subQ95,subQ97,subQ99])],"isStart":false}),makeQuery(id+"F18.opExtrude","CAP_FACE",FACE,{"disambiguationData":[OSD([sQuery(id+"F17.wireOp",EDGE,"E47.bottom"),subQ104,subQ106,subQ16,subQ103,subQ108,subQ12,sQuery(id+"F17.wireOp",EDGE,"E49.top"),subQ11,subQ7])],"isStart":false}),makeQuery(id+"F18.opExtrude","CAP_FACE",FACE,{"disambiguationData":[OSD([subQ110,subQ112,sQuery(id+"F17.wireOp",EDGE,"E50.left"),sQuery(id+"F17.wireOp",EDGE,"E50.right")])],"isStart":false})]})})});}
            var sketch = newSketch(context, id + "F24", { "sketchPlane" : qUnion([Q0])});
            skLineSegment(sketch, "E58.bottom", {"start": v(-10810, -12310) * mm, "end": v(-7900, -12310) * mm});
            skLineSegment(sketch, "E58.top", {"start": v(-10810, -8400) * mm, "end": v(-7900, -8400) * mm});
            skLineSegment(sketch, "E58.left", {"start": v(-10810, -12310) * mm, "end": v(-10810, -8400) * mm});
            skLineSegment(sketch, "E58.right", {"start": v(-7900, -12310) * mm, "end": v(-7900, -8400) * mm});
            skSolve(sketch);
        }
        {
            var Q0;
            Q0=makeQuery(id+"F24.imprint","IMPRINT",FACE,{"disambiguationData":[TD([[makeQuery(id+"F24.imprint","IMPRINT",EDGE,{"derivedFrom":sQuery(id+"F24.wireOp",EDGE,"E58.bottom")}),1.0]])]});
            extrude(context, id + "F25", {"entities" : qUnion([Q0]), "operationType" : NewBodyOperationType.REMOVE, "oppositeDirection" : true, "depth" : 4000 * mm, "offsetDistance" : 25 * mm});
        }
    });